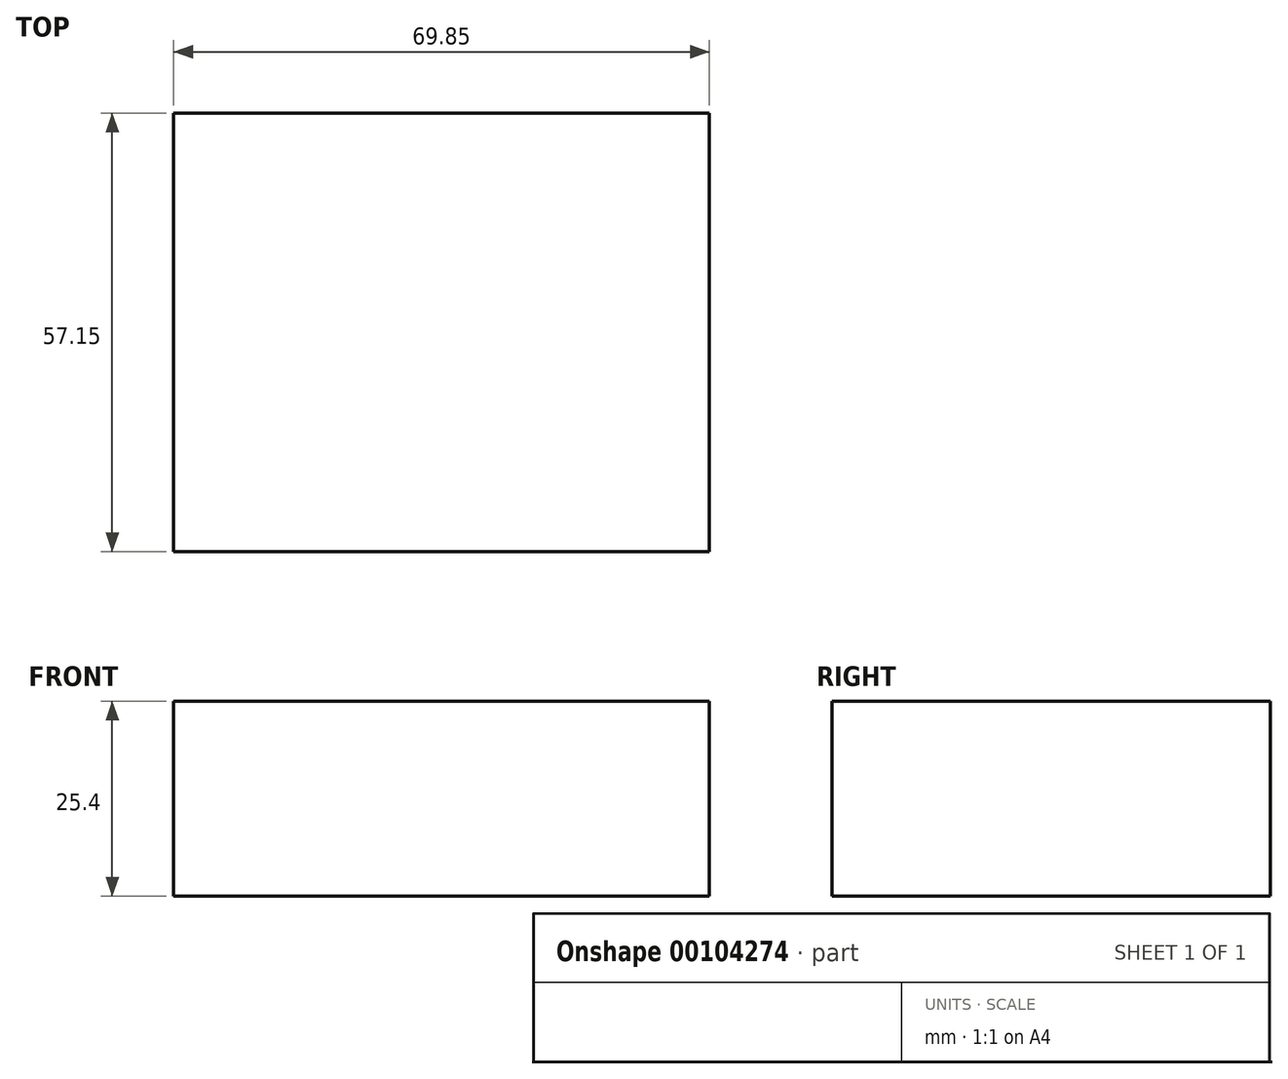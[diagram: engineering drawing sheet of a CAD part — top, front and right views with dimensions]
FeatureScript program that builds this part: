
annotation { "Feature Type Name" : "Feature", "Feature Type Description" : "" }
export const myFeature = defineFeature(function(context is Context, id is Id, definition is map)
    precondition{}
    {
        {
            var Q0;
            Q0=qCreatedBy(makeId("Top.planeOp"),FACE);
            var sketch = newSketch(context, id + "F0", { "sketchPlane" : qUnion([Q0])});
            skLineSegment(sketch, "E0.bottom", {"start": v(-32.99, 44.97) * mm, "end": v(36.86, 44.97) * mm});
            skLineSegment(sketch, "E0.top", {"start": v(-32.99, -12.18) * mm, "end": v(36.86, -12.18) * mm});
            skLineSegment(sketch, "E0.left", {"start": v(-32.99, 44.97) * mm, "end": v(-32.99, -12.18) * mm});
            skLineSegment(sketch, "E0.right", {"start": v(36.86, 44.97) * mm, "end": v(36.86, -12.18) * mm});
            skSolve(sketch);
        }
        {
            var Q0;
            Q0=makeQuery(id+"F0.imprint","IMPRINT",FACE,{"disambiguationData":[TD([[makeQuery(id+"F0.imprint","IMPRINT",EDGE,{"derivedFrom":sQuery(id+"F0.wireOp",EDGE,"E0.bottom")}),-1.0]])]});
            extrude(context, id + "F1", {"entities" : qUnion([Q0]), "depth" : 25.4 * mm});
        }
    });
